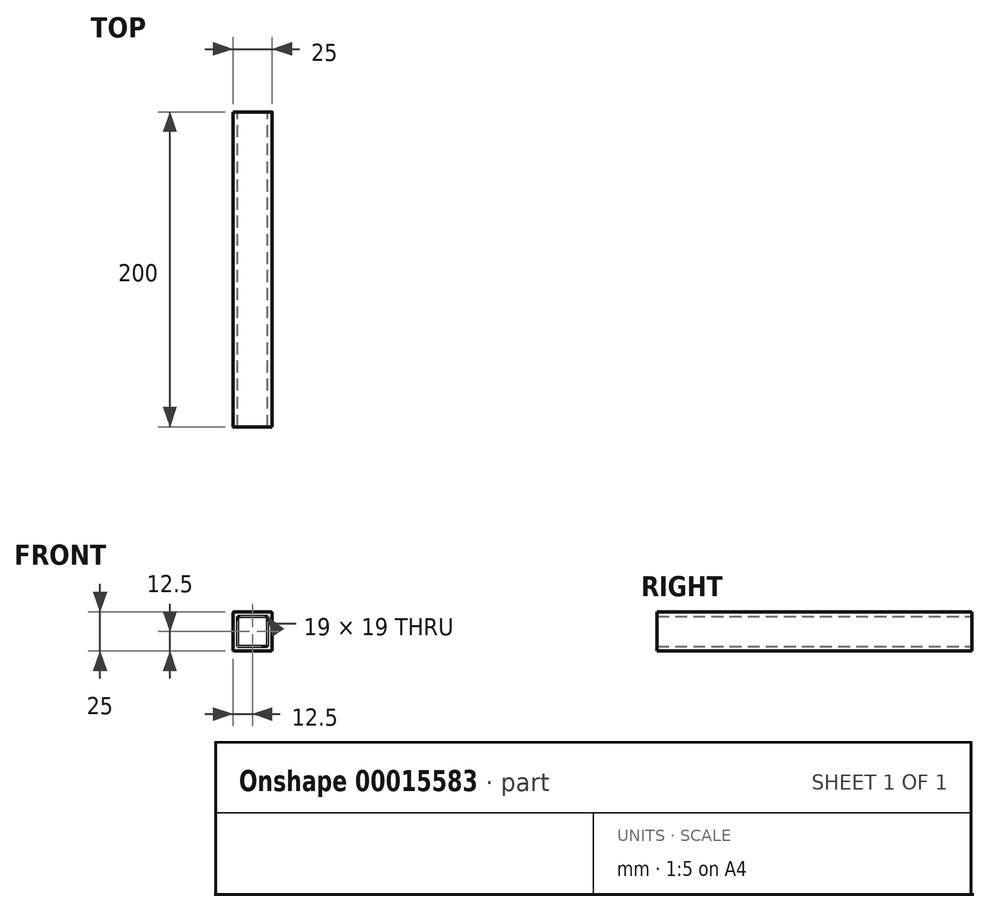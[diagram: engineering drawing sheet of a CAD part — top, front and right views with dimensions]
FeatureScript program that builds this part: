
annotation { "Feature Type Name" : "Feature", "Feature Type Description" : "" }
export const myFeature = defineFeature(function(context is Context, id is Id, definition is map)
    precondition{}
    {
        {
            var Q0;
            Q0=qCreatedBy(makeId("Front.planeOp"),FACE);
            var sketch = newSketch(context, id + "F0", { "sketchPlane" : qUnion([Q0])});
            skLineSegment(sketch, "E0.bottom", {"start": v(1, 0) * mm, "end": v(24, 0) * mm});
            skLineSegment(sketch, "E0.top", {"start": v(1, 25) * mm, "end": v(24, 25) * mm});
            skLineSegment(sketch, "E0.left", {"start": v(0, 1) * mm, "end": v(0, 24) * mm});
            skLineSegment(sketch, "E0.right", {"start": v(25, 1) * mm, "end": v(25, 24) * mm});
            skPoint(sketch, "E1.visualSharp", {"position": v(0, 25) * mm});
            skArc(sketch, "E1.filletArc", {"start": v(1, 25) * mm, "mid": v(0.3, 24.7) * mm, "end": v(0, 24) * mm});
            skPoint(sketch, "E2.visualSharp", {"position": v(0, 0) * mm});
            skArc(sketch, "E2.filletArc", {"start": v(0, 1) * mm, "mid": v(0.3, 0.3) * mm, "end": v(1, 0) * mm});
            skPoint(sketch, "E3.visualSharp", {"position": v(25, 25) * mm});
            skArc(sketch, "E3.filletArc", {"start": v(25, 24) * mm, "mid": v(24.7, 24.7) * mm, "end": v(24, 25) * mm});
            skPoint(sketch, "E4.visualSharp", {"position": v(25, 0) * mm});
            skArc(sketch, "E4.filletArc", {"start": v(24, 0) * mm, "mid": v(24.7, 0.3) * mm, "end": v(25, 1) * mm});
            skLineSegment(sketch, "E5.0", {"start": v(3, 3) * mm, "end": v(3, 22) * mm});
            skLineSegment(sketch, "E5.1", {"start": v(3, 3) * mm, "end": v(22, 3) * mm});
            skLineSegment(sketch, "E5.2", {"start": v(22, 3) * mm, "end": v(22, 22) * mm});
            skLineSegment(sketch, "E5.3", {"start": v(3, 22) * mm, "end": v(22, 22) * mm});
            skSolve(sketch);
        }
        {
            var Q0;
            Q0=makeQuery(id+"F0.imprint","IMPRINT",FACE,{"disambiguationData":[TD([[makeQuery(id+"F0.imprint","IMPRINT",EDGE,{"derivedFrom":sQuery(id+"F0.wireOp",EDGE,"E0.bottom")}),1.0]])]});
            extrude(context, id + "F1", {"entities" : qUnion([Q0]), "depth" : 200 * mm});
        }
    });
